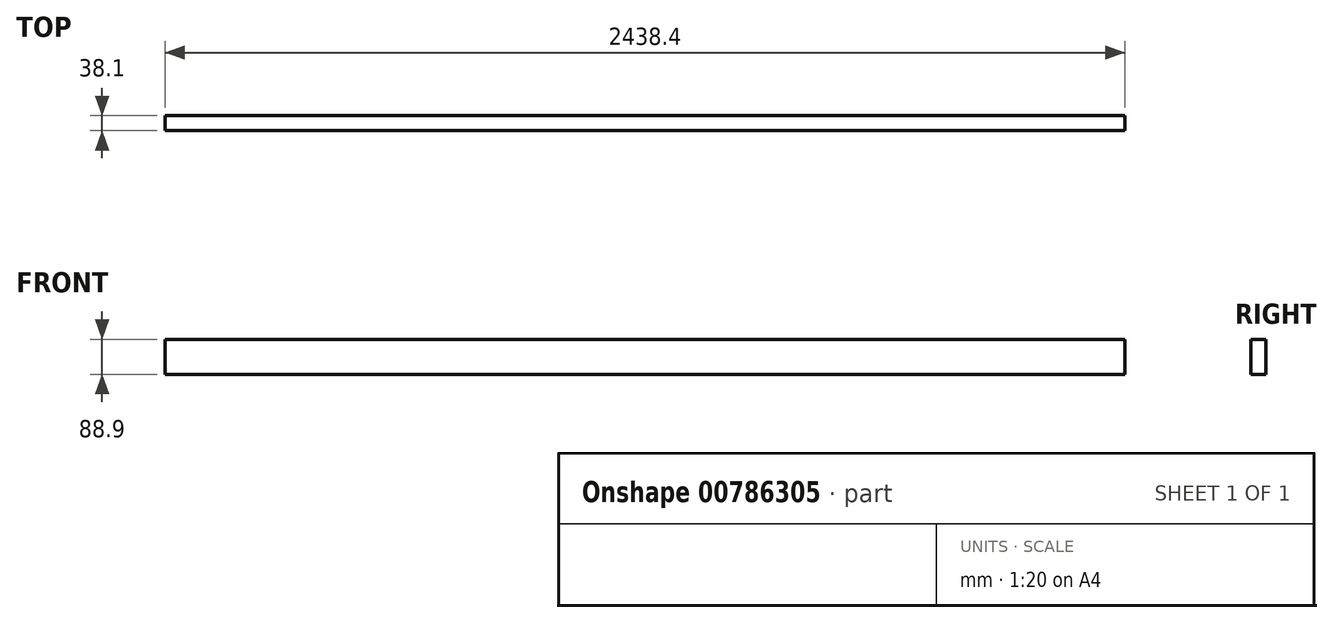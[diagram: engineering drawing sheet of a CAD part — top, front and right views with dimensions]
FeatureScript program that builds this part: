
annotation { "Feature Type Name" : "Feature", "Feature Type Description" : "" }
export const myFeature = defineFeature(function(context is Context, id is Id, definition is map)
    precondition{}
    {
        {
            var Q0;
            Q0=qCreatedBy(makeId("Front.planeOp"),FACE);
            var sketch = newSketch(context, id + "F0", { "sketchPlane" : qUnion([Q0])});
            skLineSegment(sketch, "E0.bottom", {"start": v(-1219.2, 44.45) * mm, "end": v(1219.2, 44.45) * mm});
            skLineSegment(sketch, "E0.top", {"start": v(-1219.2, -44.45) * mm, "end": v(1219.2, -44.45) * mm});
            skLineSegment(sketch, "E0.left", {"start": v(-1219.2, 44.45) * mm, "end": v(-1219.2, -44.45) * mm});
            skLineSegment(sketch, "E0.right", {"start": v(1219.2, 44.45) * mm, "end": v(1219.2, -44.45) * mm});
            skPoint(sketch, "E0.middle", {"position": v(0, 0) * mm});
            skSolve(sketch);
        }
        {
            var Q0;
            Q0=makeQuery(id+"F0.imprint","IMPRINT",FACE,{"disambiguationData":[TD([[makeQuery(id+"F0.imprint","IMPRINT",EDGE,{"derivedFrom":sQuery(id+"F0.wireOp",EDGE,"E0.bottom")}),-1.0]])]});
            extrude(context, id + "F1", {"entities" : qUnion([Q0]), "endBound" : BoundingType.SYMMETRIC, "depth" : 38.1 * mm, "offsetDistance" : 25.4 * mm});
        }
    });
